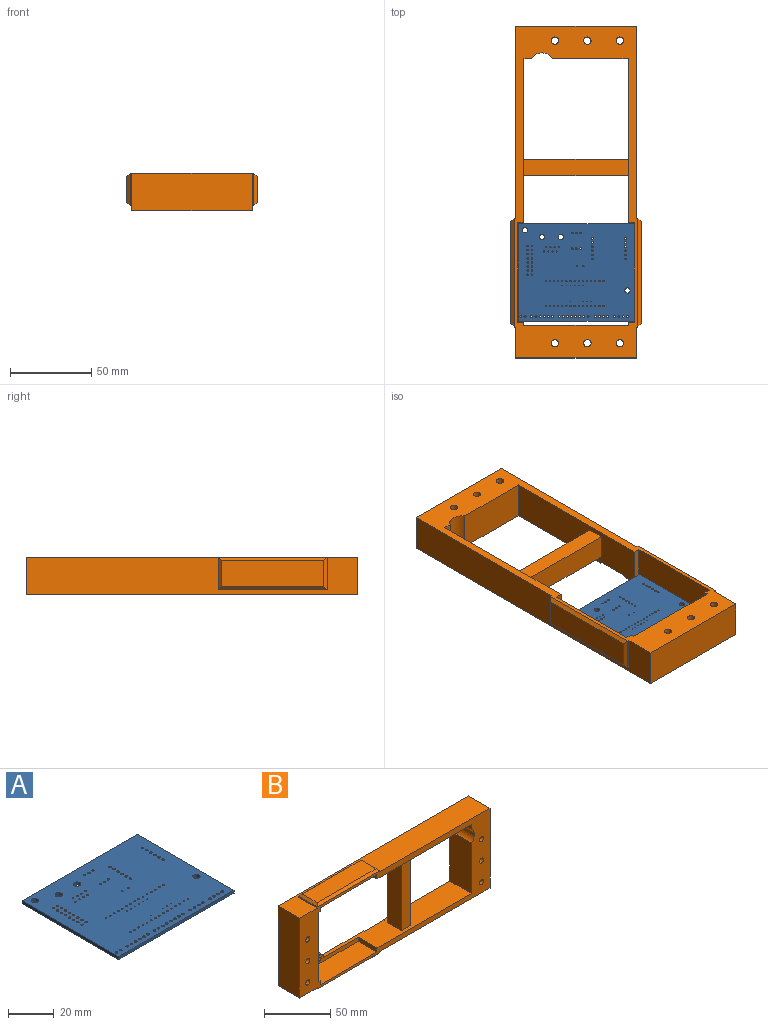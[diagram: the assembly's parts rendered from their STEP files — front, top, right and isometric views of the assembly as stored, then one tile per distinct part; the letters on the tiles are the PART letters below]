
ASSEMBLY  parts=2 mates=1
PART A: 118 faces, bbox 71.3x60x1.6 mm
  f0: plane 71.25x1.6mm, normal (0,-1,0), area 114mm2, adj f1,f2,f3,f4
  f1: plane 60x1.6mm, normal (1,0,0), area 96mm2, adj f0,f3,f4,f5
  f2: plane 60x1.6mm, normal (-1,0,0), area 96mm2, adj f0,f3,f4,f5
  f3: plane 71.25x60mm, normal (0,0,-1), area 4162.2mm2, adj f0,f1,f2,f5,f6,f7,f8,f9
  f4: plane 71.25x60mm, normal (0,0,1), area 4162.2mm2, adj f0,f1,f2,f5,f6,f7,f8,f9
  f5: plane 71.25x1.6mm, normal (0,1,0), area 114mm2, adj f1,f2,f3,f4
  f6: cylinder r=0.38mm len=1.6mm, axis (0,0,1), area 3.8mm2, adj f3,f4
  f7: cylinder r=0.62mm len=1.6mm, axis (0,0,1), area 6.3mm2, adj f3,f4
  f8: cylinder r=0.62mm len=1.6mm, axis (0,0,1), area 6.3mm2, adj f3,f4
  f9: cylinder r=0.62mm len=1.6mm, axis (0,0,1), area 6.3mm2, adj f3,f4
  f10: cylinder r=0.62mm len=1.6mm, axis (0,0,1), area 6.3mm2, adj f3,f4
  f11: cylinder r=0.62mm len=1.6mm, axis (0,0,1), area 6.3mm2, adj f3,f4
  f12: cylinder r=1.6mm len=3.2mm, axis (0,0,1), area 16.1mm2, adj f3,f4
  f13: cylinder r=0.51mm len=1.6mm, axis (0,0,1), area 5.1mm2, adj f3,f4
  f14: cylinder r=0.51mm len=1.6mm, axis (0,0,1), area 5.1mm2, adj f3,f4
  f15: cylinder r=0.51mm len=1.6mm, axis (0,0,1), area 5.1mm2, adj f3,f4
  f16: cylinder r=0.51mm len=1.6mm, axis (0,0,1), area 5.1mm2, adj f3,f4
  f17: cylinder r=0.51mm len=1.6mm, axis (0,0,1), area 5.1mm2, adj f3,f4
  f18: cylinder r=0.51mm len=1.6mm, axis (0,0,1), area 5.1mm2, adj f3,f4
  f19: cylinder r=0.51mm len=1.6mm, axis (0,0,1), area 5.1mm2, adj f3,f4
  f20: cylinder r=0.51mm len=1.6mm, axis (0,0,1), area 5.1mm2, adj f3,f4
  f21: cylinder r=0.51mm len=1.6mm, axis (0,0,1), area 5.1mm2, adj f3,f4
  f22: cylinder r=0.51mm len=1.6mm, axis (0,0,1), area 5.1mm2, adj f3,f4
  f23: cylinder r=0.51mm len=1.6mm, axis (0,0,1), area 5.1mm2, adj f3,f4
  f24: cylinder r=0.51mm len=1.6mm, axis (0,0,1), area 5.1mm2, adj f3,f4
  f25: cylinder r=0.51mm len=1.6mm, axis (0,0,1), area 5.1mm2, adj f3,f4
  f26: cylinder r=0.51mm len=1.6mm, axis (0,0,1), area 5.1mm2, adj f3,f4
  f27: cylinder r=0.51mm len=1.6mm, axis (0,0,1), area 5.1mm2, adj f3,f4
  f28: cylinder r=0.51mm len=1.6mm, axis (0,0,1), area 5.1mm2, adj f3,f4
  f29: cylinder r=1.6mm len=3.2mm, axis (0,0,1), area 16.1mm2, adj f3,f4
  f30: cylinder r=0.4mm len=1.6mm, axis (0,0,1), area 4mm2, adj f3,f4
  f31: cylinder r=0.38mm len=1.6mm, axis (0,0,1), area 3.8mm2, adj f3,f4
  f32: cylinder r=0.4mm len=1.6mm, axis (0,0,1), area 4mm2, adj f3,f4
  f33: cylinder r=0.38mm len=1.6mm, axis (0,0,1), area 3.8mm2, adj f3,f4
  f34: cylinder r=0.62mm len=1.6mm, axis (0,0,1), area 6.3mm2, adj f3,f4
  f35: cylinder r=0.4mm len=1.6mm, axis (0,0,1), area 4mm2, adj f3,f4
  f36: cylinder r=0.4mm len=1.6mm, axis (0,0,1), area 4mm2, adj f3,f4
  f37: cylinder r=0.4mm len=1.6mm, axis (0,0,1), area 4mm2, adj f3,f4
  f38: cylinder r=0.4mm len=1.6mm, axis (0,0,1), area 4mm2, adj f3,f4
  f39: cylinder r=0.4mm len=1.6mm, axis (0,0,1), area 4mm2, adj f3,f4
  f40: cylinder r=0.4mm len=1.6mm, axis (0,0,1), area 4mm2, adj f3,f4
  f41: cylinder r=0.25mm len=1.6mm, axis (0,0,1), area 2.5mm2, adj f3,f4
  f42: cylinder r=0.25mm len=1.6mm, axis (0,0,1), area 2.5mm2, adj f3,f4
  f43: cylinder r=0.25mm len=1.6mm, axis (0,0,1), area 2.5mm2, adj f3,f4
  f44: cylinder r=0.4mm len=1.6mm, axis (0,0,1), area 4mm2, adj f3,f4
  f45: cylinder r=0.4mm len=1.6mm, axis (0,0,1), area 4mm2, adj f3,f4
  f46: cylinder r=0.4mm len=1.6mm, axis (0,0,1), area 4mm2, adj f3,f4
  f47: cylinder r=0.4mm len=1.6mm, axis (0,0,1), area 4mm2, adj f3,f4
  f48: cylinder r=0.25mm len=1.6mm, axis (0,0,1), area 2.5mm2, adj f3,f4
  f49: cylinder r=0.25mm len=1.6mm, axis (0,0,1), area 2.5mm2, adj f3,f4
  f50: cylinder r=0.4mm len=1.6mm, axis (0,0,1), area 4mm2, adj f3,f4
  f51: cylinder r=0.4mm len=1.6mm, axis (0,0,1), area 4mm2, adj f3,f4
  f52: cylinder r=0.25mm len=1.6mm, axis (0,0,1), area 2.5mm2, adj f3,f4
  f53: cylinder r=0.25mm len=1.6mm, axis (0,0,1), area 2.5mm2, adj f3,f4
  f54: cylinder r=0.4mm len=1.6mm, axis (0,0,1), area 4mm2, adj f3,f4
  f55: cylinder r=0.4mm len=1.6mm, axis (0,0,1), area 4mm2, adj f3,f4
  f56: cylinder r=0.25mm len=1.6mm, axis (0,0,1), area 2.5mm2, adj f3,f4
  f57: cylinder r=0.4mm len=1.6mm, axis (0,0,1), area 4mm2, adj f3,f4
  f58: cylinder r=0.25mm len=1.6mm, axis (0,0,1), area 2.5mm2, adj f3,f4
  f59: cylinder r=0.4mm len=1.6mm, axis (0,0,1), area 4mm2, adj f3,f4
  f60: cylinder r=0.4mm len=1.6mm, axis (0,0,1), area 4mm2, adj f3,f4
  f61: cylinder r=0.4mm len=1.6mm, axis (0,0,1), area 4mm2, adj f3,f4
  f62: cylinder r=0.38mm len=1.6mm, axis (0,0,1), area 3.8mm2, adj f3,f4
  f63: cylinder r=0.38mm len=1.6mm, axis (0,0,1), area 3.8mm2, adj f3,f4
  f64: cylinder r=0.4mm len=1.6mm, axis (0,0,1), area 4mm2, adj f3,f4
  f65: cylinder r=0.4mm len=1.6mm, axis (0,0,1), area 4mm2, adj f3,f4
  f66: cylinder r=0.62mm len=1.6mm, axis (0,0,1), area 6.3mm2, adj f3,f4
  f67: cylinder r=0.62mm len=1.6mm, axis (0,0,1), area 6.3mm2, adj f3,f4
  f68: cylinder r=0.62mm len=1.6mm, axis (0,0,1), area 6.3mm2, adj f3,f4
  f69: cylinder r=0.62mm len=1.6mm, axis (0,0,1), area 6.3mm2, adj f3,f4
  f70: cylinder r=0.62mm len=1.6mm, axis (0,0,1), area 6.3mm2, adj f3,f4
  f71: cylinder r=0.62mm len=1.6mm, axis (0,0,1), area 6.3mm2, adj f3,f4
  f72: cylinder r=0.62mm len=1.6mm, axis (0,0,1), area 6.3mm2, adj f3,f4
  f73: cylinder r=0.62mm len=1.6mm, axis (0,0,1), area 6.3mm2, adj f3,f4
  f74: cylinder r=0.62mm len=1.6mm, axis (0,0,1), area 6.3mm2, adj f3,f4
  f75: cylinder r=1.6mm len=3.2mm, axis (0,0,1), area 16.1mm2, adj f3,f4
  f76: cylinder r=0.38mm len=1.6mm, axis (0,0,1), area 3.8mm2, adj f3,f4
  f77: cylinder r=0.5mm len=1.6mm, axis (0,0,1), area 5mm2, adj f3,f4
  f78: cylinder r=0.5mm len=1.6mm, axis (0,0,1), area 5mm2, adj f3,f4
  f79: cylinder r=0.38mm len=1.6mm, axis (0,0,1), area 3.8mm2, adj f3,f4
  f80: cylinder r=0.5mm len=1.6mm, axis (0,0,1), area 5mm2, adj f3,f4
  f81: cylinder r=0.38mm len=1.6mm, axis (0,0,1), area 3.8mm2, adj f3,f4
  f82: cylinder r=0.4mm len=1.6mm, axis (0,0,1), area 4mm2, adj f3,f4
  f83: cylinder r=0.4mm len=1.6mm, axis (0,0,1), area 4mm2, adj f3,f4
  f84: cylinder r=0.5mm len=1.6mm, axis (0,0,1), area 5mm2, adj f3,f4
  f85: cylinder r=0.5mm len=1.6mm, axis (0,0,1), area 5mm2, adj f3,f4
  f86: cylinder r=0.5mm len=1.6mm, axis (0,0,1), area 5mm2, adj f3,f4
  f87: cylinder r=0.56mm len=1.6mm, axis (0,0,1), area 5.6mm2, adj f3,f4
  f88: cylinder r=0.56mm len=1.6mm, axis (0,0,1), area 5.6mm2, adj f3,f4
  f89: cylinder r=0.25mm len=1.6mm, axis (0,0,1), area 2.5mm2, adj f3,f4
  f90: cylinder r=0.4mm len=1.6mm, axis (0,0,1), area 4mm2, adj f3,f4
  f91: cylinder r=0.56mm len=1.6mm, axis (0,0,1), area 5.6mm2, adj f3,f4
  f92: cylinder r=0.56mm len=1.6mm, axis (0,0,1), area 5.6mm2, adj f3,f4
  f93: cylinder r=0.56mm len=1.6mm, axis (0,0,1), area 5.6mm2, adj f3,f4
  f94: cylinder r=0.4mm len=1.6mm, axis (0,0,1), area 4mm2, adj f3,f4
  f95: cylinder r=0.56mm len=1.6mm, axis (0,0,1), area 5.6mm2, adj f3,f4
  f96: cylinder r=0.56mm len=1.6mm, axis (0,0,1), area 5.6mm2, adj f3,f4
  f97: cylinder r=0.56mm len=1.6mm, axis (0,0,1), area 5.6mm2, adj f3,f4
  f98: cylinder r=0.56mm len=1.6mm, axis (0,0,1), area 5.6mm2, adj f3,f4
  f99: cylinder r=0.56mm len=1.6mm, axis (0,0,1), area 5.6mm2, adj f3,f4
  f100: cylinder r=0.56mm len=1.6mm, axis (0,0,1), area 5.6mm2, adj f3,f4
  f101: cylinder r=0.62mm len=1.6mm, axis (0,0,1), area 6.3mm2, adj f3,f4
  f102: cylinder r=0.62mm len=1.6mm, axis (0,0,1), area 6.3mm2, adj f3,f4
  f103: cylinder r=1.6mm len=3.2mm, axis (0,0,1), area 16.1mm2, adj f3,f4
  f104: cylinder r=0.62mm len=1.6mm, axis (0,0,1), area 6.3mm2, adj f3,f4
  f105: cylinder r=0.62mm len=1.6mm, axis (0,0,1), area 6.3mm2, adj f3,f4
  f106: cylinder r=0.62mm len=1.6mm, axis (0,0,1), area 6.3mm2, adj f3,f4
  f107: cylinder r=0.4mm len=1.6mm, axis (0,0,1), area 4mm2, adj f3,f4
  f108: cylinder r=0.62mm len=1.6mm, axis (0,0,1), area 6.3mm2, adj f3,f4
  f109: cylinder r=0.4mm len=1.6mm, axis (0,0,1), area 4mm2, adj f3,f4
  f110: cylinder r=0.62mm len=1.6mm, axis (0,0,1), area 6.3mm2, adj f3,f4
  f111: cylinder r=0.4mm len=1.6mm, axis (0,0,1), area 4mm2, adj f3,f4
  f112: cylinder r=0.4mm len=1.6mm, axis (0,0,1), area 4mm2, adj f3,f4
  f113: cylinder r=0.4mm len=1.6mm, axis (0,0,1), area 4mm2, adj f3,f4
  f114: cylinder r=0.4mm len=1.6mm, axis (0,0,1), area 4mm2, adj f3,f4
  f115: cylinder r=0.62mm len=1.6mm, axis (0,0,1), area 6.3mm2, adj f3,f4
  f116: cylinder r=0.56mm len=1.6mm, axis (0,0,1), area 5.6mm2, adj f3,f4
  f117: cylinder r=0.62mm len=1.6mm, axis (0,0,1), area 6.3mm2, adj f3,f4
PART B: 59 faces, bbox 204x23x80 mm
  f0: plane 46.66x23mm, normal (-1,0,0), area 1073.1mm2, adj f1,f3,f5,f58
  f1: plane 204x74mm, normal (0,1,0), area 4408.3mm2, adj f0,f2,f3,f4,f6,f7,f8,f9
  f2: plane 204x23mm, normal (0,0,-1), area 3331mm2, adj f1,f5,f6,f8,f47,f48,f49,f55
  f3: plane 138.5x23mm, normal (0,0,1), area 2264.5mm2, adj f0,f1,f5,f23,f26,f30,f35,f36
  f4: plane 101.5x23mm, normal (0,0,-1), area 2174.5mm2, adj f1,f5,f16,f19,f22,f29,f35,f36
  f5: plane 204x76mm, normal (0,-1,0), area 4149.7mm2, adj f0,f2,f3,f4,f6,f7,f8,f9
  f6: plane 74x23mm, normal (1,0,0), area 1702mm2, adj f1,f2,f5,f7
  f7: plane 204x23mm, normal (0,0,1), area 3352mm2, adj f1,f5,f6,f8,f39,f40,f41
  f8: plane 74x23mm, normal (-1,0,0), area 1702mm2, adj f1,f2,f5,f7
  f9: cylinder r=2.25mm len=23mm, axis (0,1,0), area 325.2mm2, adj f1,f5
  f10: cylinder r=2.25mm len=23mm, axis (0,1,0), area 325.2mm2, adj f1,f5
  f11: cylinder r=2.25mm len=23mm, axis (0,1,0), area 325.2mm2, adj f1,f5
  f12: cylinder r=2.25mm len=23mm, axis (0,1,0), area 325.2mm2, adj f1,f5
  f13: cylinder r=2.25mm len=23mm, axis (0,1,0), area 325.2mm2, adj f1,f5
  f14: cylinder r=2.25mm len=23mm, axis (0,1,0), area 325.2mm2, adj f1,f5
  f15: plane 23x17.5mm, normal (0,0,1), area 92.5mm2, adj f1,f5,f18,f24,f26,f32
  f16: plane 23x4.66mm, normal (-1,0,0), area 107.1mm2, adj f1,f4,f5,f58
  f17: plane 54.5x23mm, normal (0,0,-1), area 203.5mm2, adj f1,f5,f18,f19,f21,f27
  f18: plane 64x23mm, normal (1,0,0), area 1472mm2, adj f1,f5,f15,f17
  f19: plane 61x8.38mm, normal (0,-1,0), area 249.8mm2, adj f4,f17,f20,f21,f22,f27,f28,f29
  f20: plane 61x20mm, normal (0,0,-1), area 1220mm2, adj f5,f19,f21,f22
  f21: plane 20x3.75mm, normal (1,0,0), area 75mm2, adj f5,f17,f19,f20
  f22: plane 20x3.75mm, normal (-1,0,0), area 75mm2, adj f4,f5,f19,f20
  f23: plane 20x3.75mm, normal (-1,0,0), area 75mm2, adj f3,f5,f25,f26
  f24: plane 20x3.75mm, normal (1,0,0), area 75mm2, adj f5,f15,f25,f26
  f25: plane 61x20mm, normal (0,0,1), area 1220mm2, adj f5,f23,f24,f26
  f26: plane 61x8.13mm, normal (0,-1,0), area 247.8mm2, adj f3,f15,f23,f24,f25,f30,f31,f32
  f27: plane 3x0.63mm, normal (-1,0,0), area 1.9mm2, adj f1,f17,f19,f28
  f28: cylinder r=4mm len=8mm, axis (0,-1,0), area 37.7mm2, adj f1,f19,f27,f29
  f29: plane 3x0.63mm, normal (1,0,0), area 1.9mm2, adj f1,f4,f19,f28
  f30: plane 3x0.38mm, normal (1,0,0), area 1.1mm2, adj f1,f3,f26,f31
  f31: cylinder r=4mm len=8mm, axis (0,-1,0), area 37.7mm2, adj f1,f26,f30,f32
  f32: plane 3x0.38mm, normal (-1,0,0), area 1.1mm2, adj f1,f15,f26,f31
  f33: cylinder r=1.7mm len=3.4mm, axis (0,-1,0), area 32mm2, adj f1,f26
  f34: cylinder r=1.7mm len=3.4mm, axis (0,-1,0), area 32mm2, adj f1,f19
  f35: plane 64x15mm, normal (1,0,0), area 960mm2, adj f3,f4,f37,f38
  f36: plane 64x15mm, normal (-1,0,0), area 960mm2, adj f3,f4,f37,f38
  f37: plane 64x10mm, normal (0,-1,0), area 640mm2, adj f3,f4,f35,f36
  f38: plane 64x10mm, normal (0,1,0), area 640mm2, adj f3,f4,f35,f36
  f39: plane 67x1mm, normal (0,1,0), area 67mm2, adj f7,f40,f41,f44
  f40: plane 20x1mm, normal (-1,0,0), area 20mm2, adj f5,f7,f39,f43
  f41: plane 20x1mm, normal (1,0,0), area 20mm2, adj f5,f7,f39,f46
  f42: plane 63x16mm, normal (0,0,1), area 1008mm2, adj f43,f44,f45,f46
  f43: plane 20x2mm, normal (-0.71,0,0.71), area 50.9mm2, adj f40,f42,f44,f45
  f44: plane 67x2mm, normal (0,0.71,0.71), area 183.8mm2, adj f39,f42,f43,f46
  f45: plane 67x2mm, normal (0,-0.71,0.71), area 183.8mm2, adj f5,f42,f43,f46
  f46: plane 20x2mm, normal (0.71,0,0.71), area 50.9mm2, adj f41,f42,f44,f45
  f47: plane 20x1mm, normal (-1,0,0), area 20mm2, adj f2,f5,f48,f54
  f48: plane 67x1mm, normal (0,1,0), area 67mm2, adj f2,f47,f49,f52
  f49: plane 20x1mm, normal (1,0,0), area 20mm2, adj f2,f5,f48,f51
  f50: plane 63x16mm, normal (0,0,-1), area 1008mm2, adj f51,f52,f53,f54
  f51: plane 20x2mm, normal (0.71,0,-0.71), area 50.9mm2, adj f49,f50,f52,f53
  f52: plane 67x2mm, normal (0,0.71,-0.71), area 183.8mm2, adj f48,f50,f51,f54
  f53: plane 67x2mm, normal (0,-0.71,-0.71), area 183.8mm2, adj f5,f50,f51,f54
  f54: plane 20x2mm, normal (-0.71,0,-0.71), area 50.9mm2, adj f47,f50,f52,f53
  f55: plane 5x1mm, normal (-1,0,0), area 5mm2, adj f1,f2,f3,f57
  f56: plane 5x1mm, normal (1,0,0), area 5mm2, adj f1,f2,f3,f57
  f57: plane 21x5mm, normal (0,1,0), area 105mm2, adj f2,f3,f55,f56
  f58: cylinder r=7.5mm len=23mm, axis (0,-1,0), area 347.8mm2, adj f0,f1,f5,f16
PLACE A t=(16.94,-5.31,8.34)mm
PLACE B rot(axis=(-0.58,-0.58,0.58),120deg) t=(52.31,74.19,5.34)mm
MATE fastened B.f28 <-> A.f12  axis (0,0,1) through (20.94,50.69,8.34)mm
